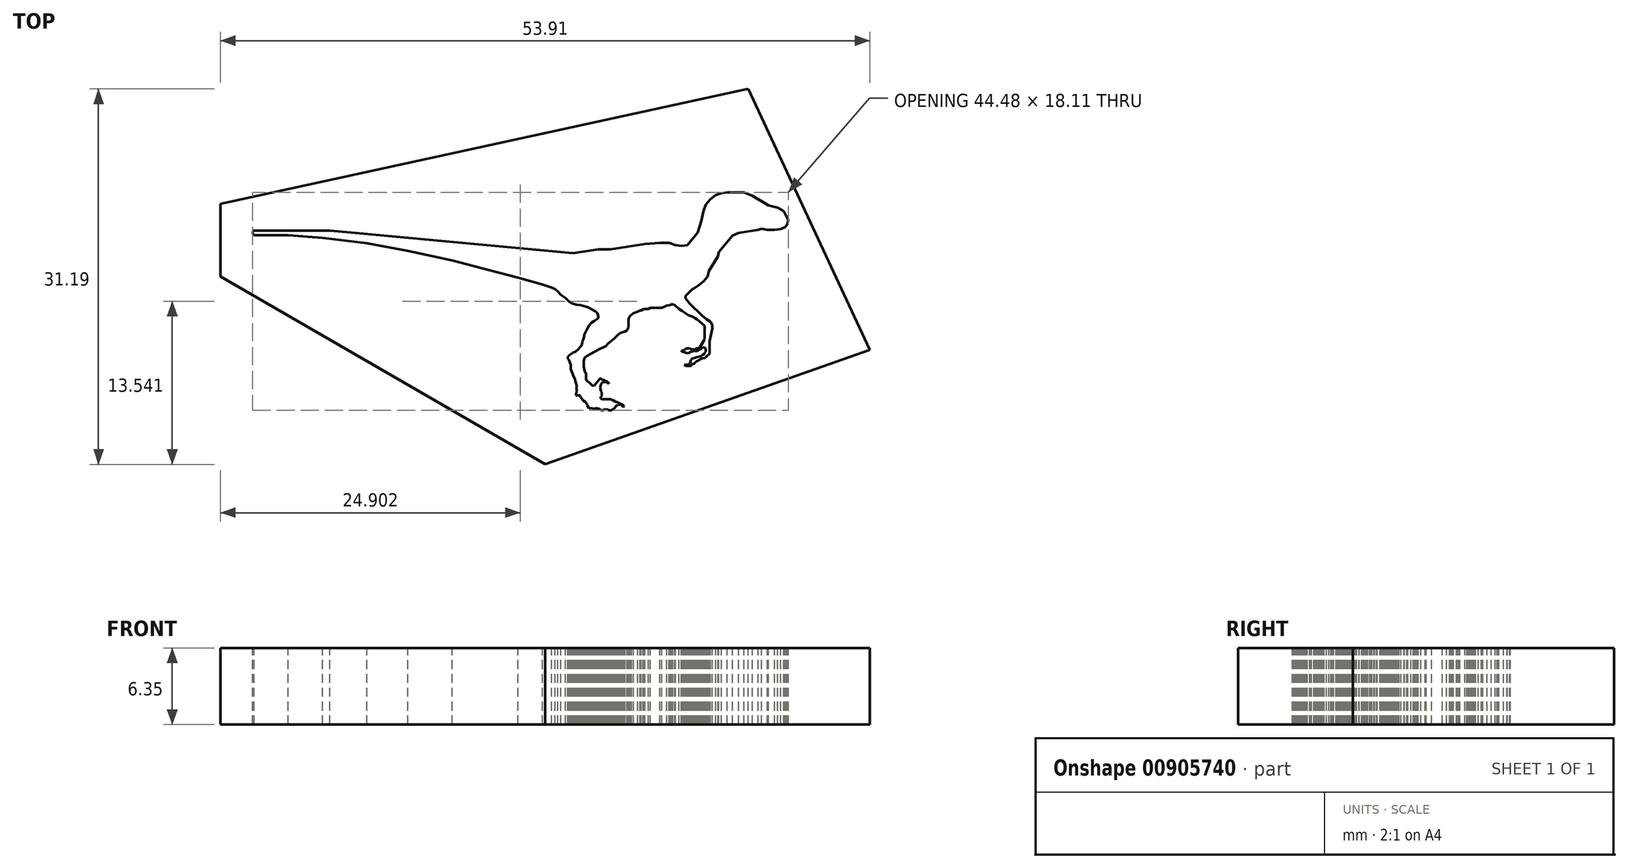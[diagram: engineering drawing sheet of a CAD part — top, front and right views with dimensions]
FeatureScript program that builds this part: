
annotation { "Feature Type Name" : "Feature", "Feature Type Description" : "" }
export const myFeature = defineFeature(function(context is Context, id is Id, definition is map)
    precondition{}
    {
        {
            var Q0;
            Q0=qCreatedBy(makeId("Top.planeOp"),FACE);
            var sketch = newSketch(context, id + "F0", { "sketchPlane" : qUnion([Q0])});
            skLineSegment(sketch, "E0", {"start": v(-51.18, -22.67) * mm, "end": v(-48.07, -22.67) * mm});
            skLineSegment(sketch, "E1", {"start": v(-48.07, -22.67) * mm, "end": v(-44.84, -22.67) * mm});
            skLineSegment(sketch, "E2", {"start": v(-44.84, -22.67) * mm, "end": v(-42.38, -22.91) * mm});
            skLineSegment(sketch, "E3", {"start": v(-42.38, -22.91) * mm, "end": v(-36.65, -23.44) * mm});
            skLineSegment(sketch, "E4", {"start": v(-36.65, -23.44) * mm, "end": v(-29.92, -24.07) * mm});
            skLineSegment(sketch, "E5", {"start": v(-29.92, -24.07) * mm, "end": v(-24.63, -24.56) * mm});
            skLineSegment(sketch, "E6", {"start": v(-24.63, -24.56) * mm, "end": v(-23.02, -24.3) * mm});
            skLineSegment(sketch, "E7", {"start": v(-23.02, -24.3) * mm, "end": v(-22.54, -24.23) * mm});
            skLineSegment(sketch, "E8", {"start": v(-22.54, -24.23) * mm, "end": v(-21.51, -24.23) * mm});
            skLineSegment(sketch, "E9", {"start": v(-21.51, -24.23) * mm, "end": v(-20.6, -24.1) * mm});
            skLineSegment(sketch, "E10", {"start": v(-20.6, -24.1) * mm, "end": v(-18.67, -23.8) * mm});
            skLineSegment(sketch, "E11", {"start": v(-18.67, -23.8) * mm, "end": v(-17.43, -23.7) * mm});
            skLineSegment(sketch, "E12", {"start": v(-17.43, -23.7) * mm, "end": v(-16.67, -23.7) * mm});
            skLineSegment(sketch, "E13", {"start": v(-16.67, -23.7) * mm, "end": v(-16.12, -23.88) * mm});
            skLineSegment(sketch, "E14", {"start": v(-16.12, -23.88) * mm, "end": v(-15.62, -23.96) * mm});
            skLineSegment(sketch, "E15", {"start": v(-15.62, -23.96) * mm, "end": v(-15.15, -23.89) * mm});
            skLineSegment(sketch, "E16", {"start": v(-15.15, -23.89) * mm, "end": v(-14.64, -23.27) * mm});
            skLineSegment(sketch, "E17", {"start": v(-14.64, -23.27) * mm, "end": v(-14.27, -22.84) * mm});
            skLineSegment(sketch, "E18", {"start": v(-14.27, -22.84) * mm, "end": v(-14.02, -21.91) * mm});
            skLineSegment(sketch, "E19", {"start": v(-14.02, -21.91) * mm, "end": v(-13.82, -21.07) * mm});
            skLineSegment(sketch, "E20", {"start": v(-13.82, -21.07) * mm, "end": v(-13.62, -20.52) * mm});
            skLineSegment(sketch, "E21", {"start": v(-13.62, -20.52) * mm, "end": v(-13.25, -20.08) * mm});
            skLineSegment(sketch, "E22", {"start": v(-13.25, -20.08) * mm, "end": v(-12.78, -19.74) * mm});
            skLineSegment(sketch, "E23", {"start": v(-12.78, -19.74) * mm, "end": v(-12.33, -19.58) * mm});
            skLineSegment(sketch, "E24", {"start": v(-12.33, -19.58) * mm, "end": v(-11.85, -19.5) * mm});
            skLineSegment(sketch, "E25", {"start": v(-11.85, -19.5) * mm, "end": v(-11.24, -19.5) * mm});
            skLineSegment(sketch, "E26", {"start": v(-11.24, -19.5) * mm, "end": v(-10.44, -19.5) * mm});
            skLineSegment(sketch, "E27", {"start": v(-10.44, -19.5) * mm, "end": v(-9.76, -19.8) * mm});
            skLineSegment(sketch, "E28", {"start": v(-9.76, -19.8) * mm, "end": v(-9.18, -20.15) * mm});
            skLineSegment(sketch, "E29", {"start": v(-9.18, -20.15) * mm, "end": v(-8.72, -20.42) * mm});
            skLineSegment(sketch, "E30", {"start": v(-8.72, -20.42) * mm, "end": v(-8.41, -20.6) * mm});
            skLineSegment(sketch, "E31", {"start": v(-8.41, -20.6) * mm, "end": v(-8.14, -20.66) * mm});
            skLineSegment(sketch, "E32", {"start": v(-8.14, -20.66) * mm, "end": v(-7.64, -20.78) * mm});
            skLineSegment(sketch, "E33", {"start": v(-7.64, -20.78) * mm, "end": v(-7.15, -21.07) * mm});
            skLineSegment(sketch, "E34", {"start": v(-7.15, -21.07) * mm, "end": v(-6.95, -21.43) * mm});
            skLineSegment(sketch, "E35", {"start": v(-6.95, -21.43) * mm, "end": v(-6.77, -21.8) * mm});
            skLineSegment(sketch, "E36", {"start": v(-6.77, -21.8) * mm, "end": v(-6.86, -22.17) * mm});
            skLineSegment(sketch, "E37", {"start": v(-6.86, -22.17) * mm, "end": v(-7.05, -22.4) * mm});
            skLineSegment(sketch, "E38", {"start": v(-7.05, -22.4) * mm, "end": v(-7.39, -22.55) * mm});
            skLineSegment(sketch, "E39", {"start": v(-7.39, -22.55) * mm, "end": v(-7.9, -22.63) * mm});
            skLineSegment(sketch, "E40", {"start": v(-7.9, -22.63) * mm, "end": v(-8.5, -22.63) * mm});
            skLineSegment(sketch, "E41", {"start": v(-8.5, -22.63) * mm, "end": v(-8.99, -22.52) * mm});
            skLineSegment(sketch, "E42", {"start": v(-8.99, -22.52) * mm, "end": v(-9.29, -22.63) * mm});
            skLineSegment(sketch, "E43", {"start": v(-9.29, -22.63) * mm, "end": v(-9.7, -22.7) * mm});
            skLineSegment(sketch, "E44", {"start": v(-9.7, -22.7) * mm, "end": v(-10.44, -22.81) * mm});
            skLineSegment(sketch, "E45", {"start": v(-10.44, -22.81) * mm, "end": v(-10.89, -22.88) * mm});
            skLineSegment(sketch, "E46", {"start": v(-10.89, -22.88) * mm, "end": v(-11.4, -23.1) * mm});
            skLineSegment(sketch, "E47", {"start": v(-11.4, -23.1) * mm, "end": v(-12.04, -23.86) * mm});
            skLineSegment(sketch, "E48", {"start": v(-12.04, -23.86) * mm, "end": v(-12.54, -24.46) * mm});
            skLineSegment(sketch, "E49", {"start": v(-12.54, -24.46) * mm, "end": v(-12.62, -24.81) * mm});
            skLineSegment(sketch, "E50", {"start": v(-12.62, -24.81) * mm, "end": v(-13.07, -25.57) * mm});
            skLineSegment(sketch, "E51", {"start": v(-13.07, -25.57) * mm, "end": v(-13.36, -26.05) * mm});
            skLineSegment(sketch, "E52", {"start": v(-13.36, -26.05) * mm, "end": v(-13.46, -26.49) * mm});
            skLineSegment(sketch, "E53", {"start": v(-13.46, -26.49) * mm, "end": v(-13.82, -26.92) * mm});
            skLineSegment(sketch, "E54", {"start": v(-13.82, -26.92) * mm, "end": v(-14.25, -27.26) * mm});
            skLineSegment(sketch, "E55", {"start": v(-14.25, -27.26) * mm, "end": v(-14.54, -27.45) * mm});
            skLineSegment(sketch, "E56", {"start": v(-14.54, -27.45) * mm, "end": v(-14.77, -27.57) * mm});
            skLineSegment(sketch, "E57", {"start": v(-14.77, -27.57) * mm, "end": v(-15.31, -28.12) * mm});
            skLineSegment(sketch, "E58", {"start": v(-15.31, -28.12) * mm, "end": v(-15.31, -28.32) * mm});
            skLineSegment(sketch, "E59", {"start": v(-15.31, -28.32) * mm, "end": v(-14.96, -28.73) * mm});
            skLineSegment(sketch, "E60", {"start": v(-14.96, -28.73) * mm, "end": v(-13.95, -29.72) * mm});
            skLineSegment(sketch, "E61", {"start": v(-13.95, -29.72) * mm, "end": v(-13.56, -30.04) * mm});
            skLineSegment(sketch, "E62", {"start": v(-13.56, -30.04) * mm, "end": v(-13.23, -30.24) * mm});
            skLineSegment(sketch, "E63", {"start": v(-13.23, -30.24) * mm, "end": v(-13.07, -30.54) * mm});
            skLineSegment(sketch, "E64", {"start": v(-13.07, -30.54) * mm, "end": v(-13.07, -30.85) * mm});
            skLineSegment(sketch, "E65", {"start": v(-13.07, -30.85) * mm, "end": v(-13.17, -31.24) * mm});
            skLineSegment(sketch, "E66", {"start": v(-13.17, -31.24) * mm, "end": v(-13.3, -31.85) * mm});
            skLineSegment(sketch, "E67", {"start": v(-13.3, -31.85) * mm, "end": v(-13.3, -32.58) * mm});
            skLineSegment(sketch, "E68", {"start": v(-13.3, -32.58) * mm, "end": v(-13.3, -32.91) * mm});
            skLineSegment(sketch, "E69", {"start": v(-13.3, -32.91) * mm, "end": v(-13.6, -33.17) * mm});
            skLineSegment(sketch, "E70", {"start": v(-13.6, -33.17) * mm, "end": v(-13.67, -33.25) * mm});
            skLineSegment(sketch, "E71", {"start": v(-13.67, -33.25) * mm, "end": v(-13.9, -33.29) * mm});
            skLineSegment(sketch, "E72", {"start": v(-13.9, -33.29) * mm, "end": v(-14.13, -33.4) * mm});
            skLineSegment(sketch, "E73", {"start": v(-14.13, -33.4) * mm, "end": v(-14.4, -33.55) * mm});
            skLineSegment(sketch, "E74", {"start": v(-14.4, -33.55) * mm, "end": v(-14.52, -33.65) * mm});
            skLineSegment(sketch, "E75", {"start": v(-14.52, -33.65) * mm, "end": v(-14.59, -33.74) * mm});
            skLineSegment(sketch, "E76", {"start": v(-14.59, -33.74) * mm, "end": v(-14.72, -33.76) * mm});
            skLineSegment(sketch, "E77", {"start": v(-14.72, -33.76) * mm, "end": v(-14.86, -33.92) * mm});
            skLineSegment(sketch, "E78", {"start": v(-14.86, -33.92) * mm, "end": v(-15.24, -33.92) * mm});
            skLineSegment(sketch, "E79", {"start": v(-15.24, -33.92) * mm, "end": v(-15.4, -33.83) * mm});
            skLineSegment(sketch, "E80", {"start": v(-15.4, -33.83) * mm, "end": v(-15.06, -33.83) * mm});
            skLineSegment(sketch, "E81", {"start": v(-15.06, -33.83) * mm, "end": v(-14.91, -33.65) * mm});
            skLineSegment(sketch, "E82", {"start": v(-14.91, -33.65) * mm, "end": v(-14.86, -33.44) * mm});
            skLineSegment(sketch, "E83", {"start": v(-14.86, -33.44) * mm, "end": v(-14.77, -33.33) * mm});
            skLineSegment(sketch, "E84", {"start": v(-14.77, -33.33) * mm, "end": v(-14.56, -33.26) * mm});
            skLineSegment(sketch, "E85", {"start": v(-14.56, -33.26) * mm, "end": v(-14.35, -33.18) * mm});
            skLineSegment(sketch, "E86", {"start": v(-14.35, -33.18) * mm, "end": v(-14.08, -33.14) * mm});
            skLineSegment(sketch, "E87", {"start": v(-14.08, -33.14) * mm, "end": v(-13.87, -33) * mm});
            skLineSegment(sketch, "E88", {"start": v(-13.87, -33) * mm, "end": v(-13.72, -32.91) * mm});
            skLineSegment(sketch, "E89", {"start": v(-13.72, -32.91) * mm, "end": v(-13.69, -32.78) * mm});
            skLineSegment(sketch, "E90", {"start": v(-13.69, -32.78) * mm, "end": v(-13.63, -32.75) * mm});
            skLineSegment(sketch, "E91", {"start": v(-13.63, -32.75) * mm, "end": v(-13.63, -32.5) * mm});
            skLineSegment(sketch, "E92", {"start": v(-13.63, -32.5) * mm, "end": v(-13.68, -32.43) * mm});
            skLineSegment(sketch, "E93", {"start": v(-13.68, -32.43) * mm, "end": v(-13.75, -32.39) * mm});
            skLineSegment(sketch, "E94", {"start": v(-13.75, -32.39) * mm, "end": v(-13.85, -32.37) * mm});
            skLineSegment(sketch, "E95", {"start": v(-13.85, -32.37) * mm, "end": v(-13.99, -32.48) * mm});
            skLineSegment(sketch, "E96", {"start": v(-13.99, -32.48) * mm, "end": v(-14.18, -32.58) * mm});
            skLineSegment(sketch, "E97", {"start": v(-14.18, -32.58) * mm, "end": v(-14.35, -32.73) * mm});
            skLineSegment(sketch, "E98", {"start": v(-14.35, -32.73) * mm, "end": v(-14.5, -32.7) * mm});
            skLineSegment(sketch, "E99", {"start": v(-14.5, -32.7) * mm, "end": v(-14.57, -32.66) * mm});
            skLineSegment(sketch, "E100", {"start": v(-14.57, -32.66) * mm, "end": v(-14.68, -32.68) * mm});
            skPoint(sketch, "E100.endSnap0", {"position": v(-14.54, -32.68) * mm});
            skLineSegment(sketch, "E101", {"start": v(-14.68, -32.68) * mm, "end": v(-14.7, -32.73) * mm});
            skLineSegment(sketch, "E102", {"start": v(-14.7, -32.73) * mm, "end": v(-14.88, -32.76) * mm});
            skLineSegment(sketch, "E103", {"start": v(-14.88, -32.76) * mm, "end": v(-15, -32.82) * mm});
            skLineSegment(sketch, "E104", {"start": v(-15, -32.82) * mm, "end": v(-15.1, -32.91) * mm});
            skLineSegment(sketch, "E105", {"start": v(-15.1, -32.91) * mm, "end": v(-15.2, -32.86) * mm});
            skLineSegment(sketch, "E106", {"start": v(-15.2, -32.86) * mm, "end": v(-15.53, -32.75) * mm});
            skLineSegment(sketch, "E107", {"start": v(-15.53, -32.75) * mm, "end": v(-15.63, -32.72) * mm});
            skLineSegment(sketch, "E108", {"start": v(-15.63, -32.72) * mm, "end": v(-15.64, -32.66) * mm});
            skLineSegment(sketch, "E109", {"start": v(-15.64, -32.66) * mm, "end": v(-15.43, -32.63) * mm});
            skLineSegment(sketch, "E110", {"start": v(-15.43, -32.63) * mm, "end": v(-15.23, -32.45) * mm});
            skLineSegment(sketch, "E111", {"start": v(-15.23, -32.45) * mm, "end": v(-15.03, -32.45) * mm});
            skLineSegment(sketch, "E112", {"start": v(-15.03, -32.45) * mm, "end": v(-14.88, -32.49) * mm});
            skLineSegment(sketch, "E113", {"start": v(-14.88, -32.49) * mm, "end": v(-14.77, -32.55) * mm});
            skLineSegment(sketch, "E114", {"start": v(-14.77, -32.55) * mm, "end": v(-14.64, -32.53) * mm});
            skLineSegment(sketch, "E115", {"start": v(-14.64, -32.53) * mm, "end": v(-14.52, -32.56) * mm});
            skLineSegment(sketch, "E116", {"start": v(-14.52, -32.56) * mm, "end": v(-14.46, -32.52) * mm});
            skLineSegment(sketch, "E117", {"start": v(-14.46, -32.52) * mm, "end": v(-14.35, -32.47) * mm});
            skLineSegment(sketch, "E118", {"start": v(-14.35, -32.47) * mm, "end": v(-14.13, -32.38) * mm});
            skLineSegment(sketch, "E119", {"start": v(-14.13, -32.38) * mm, "end": v(-14, -32.18) * mm});
            skLineSegment(sketch, "E120", {"start": v(-14, -32.18) * mm, "end": v(-13.91, -32.01) * mm});
            skLineSegment(sketch, "E121", {"start": v(-13.91, -32.01) * mm, "end": v(-13.82, -31.87) * mm});
            skLineSegment(sketch, "E122", {"start": v(-13.82, -31.87) * mm, "end": v(-13.76, -31.76) * mm});
            skLineSegment(sketch, "E123", {"start": v(-13.76, -31.76) * mm, "end": v(-13.72, -31.59) * mm});
            skLineSegment(sketch, "E124", {"start": v(-13.72, -31.59) * mm, "end": v(-13.72, -30.9) * mm});
            skLineSegment(sketch, "E125", {"start": v(-13.72, -30.9) * mm, "end": v(-13.72, -30.6) * mm});
            skLineSegment(sketch, "E126", {"start": v(-13.72, -30.6) * mm, "end": v(-14.34, -30.06) * mm});
            skLineSegment(sketch, "E127", {"start": v(-14.34, -30.06) * mm, "end": v(-14.52, -29.96) * mm});
            skLineSegment(sketch, "E128", {"start": v(-14.52, -29.96) * mm, "end": v(-14.73, -29.84) * mm});
            skLineSegment(sketch, "E129", {"start": v(-14.73, -29.84) * mm, "end": v(-15.08, -29.7) * mm});
            skLineSegment(sketch, "E130", {"start": v(-15.08, -29.7) * mm, "end": v(-15.3, -29.53) * mm});
            skLineSegment(sketch, "E131", {"start": v(-15.3, -29.53) * mm, "end": v(-15.58, -29.36) * mm});
            skLineSegment(sketch, "E132", {"start": v(-15.58, -29.36) * mm, "end": v(-15.83, -29.2) * mm});
            skLineSegment(sketch, "E133", {"start": v(-15.83, -29.2) * mm, "end": v(-16.18, -28.87) * mm});
            skLineSegment(sketch, "E134", {"start": v(-16.18, -28.87) * mm, "end": v(-16.34, -28.8) * mm});
            skLineSegment(sketch, "E135", {"start": v(-16.34, -28.8) * mm, "end": v(-16.48, -28.8) * mm});
            skLineSegment(sketch, "E136", {"start": v(-16.48, -28.8) * mm, "end": v(-16.6, -28.86) * mm});
            skLineSegment(sketch, "E137", {"start": v(-16.6, -28.86) * mm, "end": v(-16.86, -28.91) * mm});
            skLineSegment(sketch, "E138", {"start": v(-16.86, -28.91) * mm, "end": v(-17.04, -29) * mm});
            skLineSegment(sketch, "E139", {"start": v(-17.04, -29) * mm, "end": v(-17.28, -29.1) * mm});
            skLineSegment(sketch, "E140", {"start": v(-17.28, -29.1) * mm, "end": v(-17.74, -29.1) * mm});
            skLineSegment(sketch, "E141", {"start": v(-17.74, -29.1) * mm, "end": v(-18.05, -29.1) * mm});
            skLineSegment(sketch, "E142", {"start": v(-18.05, -29.1) * mm, "end": v(-18.24, -29.1) * mm});
            skLineSegment(sketch, "E143", {"start": v(-18.24, -29.1) * mm, "end": v(-18.37, -29.18) * mm});
            skLineSegment(sketch, "E144", {"start": v(-18.37, -29.18) * mm, "end": v(-18.53, -29.18) * mm});
            skLineSegment(sketch, "E145", {"start": v(-18.53, -29.18) * mm, "end": v(-18.73, -29.18) * mm});
            skLineSegment(sketch, "E146", {"start": v(-18.73, -29.18) * mm, "end": v(-18.83, -29.2) * mm});
            skLineSegment(sketch, "E147", {"start": v(-18.83, -29.2) * mm, "end": v(-18.99, -29.3) * mm});
            skLineSegment(sketch, "E148", {"start": v(-18.99, -29.3) * mm, "end": v(-19.1, -29.3) * mm});
            skLineSegment(sketch, "E149", {"start": v(-19.1, -29.3) * mm, "end": v(-19.28, -29.4) * mm});
            skLineSegment(sketch, "E150", {"start": v(-19.28, -29.4) * mm, "end": v(-19.61, -29.56) * mm});
            skLineSegment(sketch, "E151", {"start": v(-19.61, -29.56) * mm, "end": v(-19.78, -29.66) * mm});
            skLineSegment(sketch, "E152", {"start": v(-19.78, -29.66) * mm, "end": v(-19.9, -29.76) * mm});
            skLineSegment(sketch, "E153", {"start": v(-19.9, -29.76) * mm, "end": v(-20.05, -30.02) * mm});
            skLineSegment(sketch, "E154", {"start": v(-20.05, -30.02) * mm, "end": v(-20.05, -30.18) * mm});
            skLineSegment(sketch, "E155", {"start": v(-20.05, -30.18) * mm, "end": v(-20.05, -30.6) * mm});
            skLineSegment(sketch, "E156", {"start": v(-20.05, -30.6) * mm, "end": v(-20.08, -30.78) * mm});
            skLineSegment(sketch, "E157", {"start": v(-20.08, -30.78) * mm, "end": v(-20.16, -30.98) * mm});
            skLineSegment(sketch, "E158", {"start": v(-20.16, -30.98) * mm, "end": v(-20.32, -31.06) * mm});
            skLineSegment(sketch, "E159", {"start": v(-20.32, -31.06) * mm, "end": v(-20.53, -31.12) * mm});
            skLineSegment(sketch, "E160", {"start": v(-20.53, -31.12) * mm, "end": v(-20.74, -31.18) * mm});
            skLineSegment(sketch, "E161", {"start": v(-20.74, -31.18) * mm, "end": v(-20.94, -31.36) * mm});
            skLineSegment(sketch, "E162", {"start": v(-20.94, -31.36) * mm, "end": v(-21.2, -31.62) * mm});
            skLineSegment(sketch, "E163", {"start": v(-21.2, -31.62) * mm, "end": v(-21.76, -32.07) * mm});
            skLineSegment(sketch, "E164", {"start": v(-21.76, -32.07) * mm, "end": v(-21.92, -32.28) * mm});
            skLineSegment(sketch, "E165", {"start": v(-21.92, -32.28) * mm, "end": v(-22.5, -32.56) * mm});
            skLineSegment(sketch, "E166", {"start": v(-22.5, -32.56) * mm, "end": v(-23.14, -32.9) * mm});
            skLineSegment(sketch, "E167", {"start": v(-23.14, -32.9) * mm, "end": v(-23.5, -33.09) * mm});
            skLineSegment(sketch, "E168", {"start": v(-23.5, -33.09) * mm, "end": v(-23.7, -33.27) * mm});
            skLineSegment(sketch, "E169", {"start": v(-23.7, -33.27) * mm, "end": v(-23.75, -33.53) * mm});
            skLineSegment(sketch, "E170", {"start": v(-23.75, -33.53) * mm, "end": v(-23.75, -33.98) * mm});
            skLineSegment(sketch, "E171", {"start": v(-23.75, -33.98) * mm, "end": v(-23.69, -34.3) * mm});
            skLineSegment(sketch, "E172", {"start": v(-23.69, -34.3) * mm, "end": v(-23.55, -34.58) * mm});
            skLineSegment(sketch, "E173", {"start": v(-23.55, -34.58) * mm, "end": v(-23.55, -34.74) * mm});
            skLineSegment(sketch, "E174", {"start": v(-23.55, -34.74) * mm, "end": v(-23.55, -35) * mm});
            skLineSegment(sketch, "E175", {"start": v(-23.55, -35) * mm, "end": v(-23.48, -35.15) * mm});
            skLineSegment(sketch, "E176", {"start": v(-23.48, -35.15) * mm, "end": v(-23.26, -35.32) * mm});
            skLineSegment(sketch, "E177", {"start": v(-23.26, -35.32) * mm, "end": v(-23.04, -35.54) * mm});
            skLineSegment(sketch, "E178", {"start": v(-23.04, -35.54) * mm, "end": v(-22.9, -35.58) * mm});
            skLineSegment(sketch, "E179", {"start": v(-22.9, -35.58) * mm, "end": v(-22.69, -35.3) * mm});
            skLineSegment(sketch, "E180", {"start": v(-22.69, -35.3) * mm, "end": v(-22.58, -35.16) * mm});
            skLineSegment(sketch, "E181", {"start": v(-22.58, -35.16) * mm, "end": v(-22.5, -35.05) * mm});
            skLineSegment(sketch, "E182", {"start": v(-22.5, -35.05) * mm, "end": v(-22.4, -34.97) * mm});
            skLineSegment(sketch, "E183", {"start": v(-22.4, -34.97) * mm, "end": v(-22.32, -34.97) * mm});
            skLineSegment(sketch, "E184", {"start": v(-22.32, -34.97) * mm, "end": v(-22.21, -35.05) * mm});
            skLineSegment(sketch, "E185", {"start": v(-22.21, -35.05) * mm, "end": v(-22.06, -35.09) * mm});
            skLineSegment(sketch, "E186", {"start": v(-22.06, -35.09) * mm, "end": v(-21.98, -35.15) * mm});
            skLineSegment(sketch, "E187", {"start": v(-21.98, -35.15) * mm, "end": v(-21.85, -35.18) * mm});
            skLineSegment(sketch, "E188", {"start": v(-21.85, -35.18) * mm, "end": v(-21.64, -35.34) * mm});
            skLineSegment(sketch, "E189", {"start": v(-21.64, -35.34) * mm, "end": v(-21.66, -35.38) * mm});
            skLineSegment(sketch, "E190", {"start": v(-21.66, -35.38) * mm, "end": v(-21.82, -35.29) * mm});
            skLineSegment(sketch, "E191", {"start": v(-21.82, -35.29) * mm, "end": v(-21.9, -35.26) * mm});
            skLineSegment(sketch, "E192", {"start": v(-21.9, -35.26) * mm, "end": v(-22.04, -35.26) * mm});
            skLineSegment(sketch, "E193", {"start": v(-22.04, -35.26) * mm, "end": v(-22.14, -35.26) * mm});
            skLineSegment(sketch, "E194", {"start": v(-22.14, -35.26) * mm, "end": v(-22.26, -35.34) * mm});
            skLineSegment(sketch, "E195", {"start": v(-22.26, -35.34) * mm, "end": v(-22.34, -35.43) * mm});
            skLineSegment(sketch, "E196", {"start": v(-22.34, -35.43) * mm, "end": v(-22.36, -35.55) * mm});
            skLineSegment(sketch, "E197", {"start": v(-22.36, -35.55) * mm, "end": v(-22.4, -35.72) * mm});
            skLineSegment(sketch, "E198", {"start": v(-22.4, -35.72) * mm, "end": v(-22.31, -36) * mm});
            skLineSegment(sketch, "E199", {"start": v(-22.31, -36) * mm, "end": v(-22.25, -36.13) * mm});
            skLineSegment(sketch, "E200", {"start": v(-22.25, -36.13) * mm, "end": v(-22.25, -36.27) * mm});
            skLineSegment(sketch, "E201", {"start": v(-22.25, -36.27) * mm, "end": v(-22.25, -36.4) * mm});
            skLineSegment(sketch, "E202", {"start": v(-22.25, -36.4) * mm, "end": v(-22.34, -36.5) * mm});
            skLineSegment(sketch, "E203", {"start": v(-22.34, -36.5) * mm, "end": v(-22.35, -36.56) * mm});
            skLineSegment(sketch, "E204", {"start": v(-22.35, -36.56) * mm, "end": v(-22.35, -36.61) * mm});
            skLineSegment(sketch, "E205", {"start": v(-22.35, -36.61) * mm, "end": v(-22.3, -36.65) * mm});
            skLineSegment(sketch, "E206", {"start": v(-22.3, -36.65) * mm, "end": v(-22.23, -36.68) * mm});
            skLineSegment(sketch, "E207", {"start": v(-22.23, -36.68) * mm, "end": v(-21.98, -36.68) * mm});
            skLineSegment(sketch, "E208", {"start": v(-21.98, -36.68) * mm, "end": v(-21.7, -36.67) * mm});
            skLineSegment(sketch, "E209", {"start": v(-21.7, -36.67) * mm, "end": v(-21.57, -36.67) * mm});
            skLineSegment(sketch, "E210", {"start": v(-21.57, -36.67) * mm, "end": v(-21.32, -36.78) * mm});
            skLineSegment(sketch, "E211", {"start": v(-21.32, -36.78) * mm, "end": v(-21.14, -36.88) * mm});
            skLineSegment(sketch, "E212", {"start": v(-21.14, -36.88) * mm, "end": v(-20.97, -36.93) * mm});
            skLineSegment(sketch, "E213", {"start": v(-20.97, -36.93) * mm, "end": v(-20.9, -36.98) * mm});
            skLineSegment(sketch, "E214", {"start": v(-20.9, -36.98) * mm, "end": v(-20.76, -37.03) * mm});
            skLineSegment(sketch, "E215", {"start": v(-20.76, -37.03) * mm, "end": v(-20.56, -37.14) * mm});
            skLineSegment(sketch, "E216", {"start": v(-20.56, -37.14) * mm, "end": v(-20.47, -37.2) * mm});
            skLineSegment(sketch, "E217", {"start": v(-20.47, -37.2) * mm, "end": v(-20.37, -37.28) * mm});
            skLineSegment(sketch, "E218", {"start": v(-20.37, -37.28) * mm, "end": v(-20.41, -37.33) * mm});
            skLineSegment(sketch, "E219", {"start": v(-20.41, -37.33) * mm, "end": v(-20.51, -37.28) * mm});
            skLineSegment(sketch, "E220", {"start": v(-20.51, -37.28) * mm, "end": v(-20.59, -37.22) * mm});
            skLineSegment(sketch, "E221", {"start": v(-20.59, -37.22) * mm, "end": v(-20.66, -37.16) * mm});
            skLineSegment(sketch, "E222", {"start": v(-20.66, -37.16) * mm, "end": v(-20.76, -37.12) * mm});
            skLineSegment(sketch, "E223", {"start": v(-20.76, -37.12) * mm, "end": v(-20.82, -37.12) * mm});
            skLineSegment(sketch, "E224", {"start": v(-20.82, -37.12) * mm, "end": v(-20.87, -37.11) * mm});
            skLineSegment(sketch, "E225", {"start": v(-20.87, -37.11) * mm, "end": v(-20.92, -37.13) * mm});
            skLineSegment(sketch, "E226", {"start": v(-20.92, -37.13) * mm, "end": v(-20.96, -37.2) * mm});
            skLineSegment(sketch, "E227", {"start": v(-20.96, -37.2) * mm, "end": v(-21.04, -37.24) * mm});
            skLineSegment(sketch, "E228", {"start": v(-21.04, -37.24) * mm, "end": v(-21.1, -37.31) * mm});
            skLineSegment(sketch, "E229", {"start": v(-21.1, -37.31) * mm, "end": v(-21.23, -37.47) * mm});
            skLineSegment(sketch, "E230", {"start": v(-21.23, -37.47) * mm, "end": v(-21.38, -37.55) * mm});
            skLineSegment(sketch, "E231", {"start": v(-21.38, -37.55) * mm, "end": v(-21.42, -37.6) * mm});
            skLineSegment(sketch, "E232", {"start": v(-21.42, -37.6) * mm, "end": v(-21.55, -37.61) * mm});
            skLineSegment(sketch, "E233", {"start": v(-21.55, -37.61) * mm, "end": v(-21.67, -37.61) * mm});
            skLineSegment(sketch, "E234", {"start": v(-21.67, -37.61) * mm, "end": v(-21.7, -37.57) * mm});
            skLineSegment(sketch, "E235", {"start": v(-21.7, -37.57) * mm, "end": v(-21.78, -37.54) * mm});
            skLineSegment(sketch, "E236", {"start": v(-21.78, -37.54) * mm, "end": v(-21.95, -37.54) * mm});
            skLineSegment(sketch, "E237", {"start": v(-21.95, -37.54) * mm, "end": v(-22.03, -37.54) * mm});
            skLineSegment(sketch, "E238", {"start": v(-22.03, -37.54) * mm, "end": v(-22.1, -37.57) * mm});
            skLineSegment(sketch, "E239", {"start": v(-22.1, -37.57) * mm, "end": v(-22.15, -37.6) * mm});
            skLineSegment(sketch, "E240", {"start": v(-22.15, -37.6) * mm, "end": v(-22.25, -37.61) * mm});
            skLineSegment(sketch, "E241", {"start": v(-22.25, -37.61) * mm, "end": v(-22.31, -37.61) * mm});
            skLineSegment(sketch, "E242", {"start": v(-22.31, -37.61) * mm, "end": v(-22.37, -37.56) * mm});
            skLineSegment(sketch, "E243", {"start": v(-22.37, -37.56) * mm, "end": v(-22.45, -37.5) * mm});
            skLineSegment(sketch, "E244", {"start": v(-22.45, -37.5) * mm, "end": v(-22.55, -37.47) * mm});
            skLineSegment(sketch, "E245", {"start": v(-22.55, -37.47) * mm, "end": v(-22.62, -37.45) * mm});
            skLineSegment(sketch, "E246", {"start": v(-22.62, -37.45) * mm, "end": v(-22.7, -37.44) * mm});
            skLineSegment(sketch, "E247", {"start": v(-22.7, -37.44) * mm, "end": v(-22.79, -37.44) * mm});
            skLineSegment(sketch, "E248", {"start": v(-22.79, -37.44) * mm, "end": v(-22.83, -37.47) * mm});
            skLineSegment(sketch, "E249", {"start": v(-22.83, -37.47) * mm, "end": v(-22.98, -37.47) * mm});
            skLineSegment(sketch, "E250", {"start": v(-22.98, -37.47) * mm, "end": v(-23.04, -37.43) * mm});
            skLineSegment(sketch, "E251", {"start": v(-23.04, -37.43) * mm, "end": v(-23.23, -37.44) * mm});
            skLineSegment(sketch, "E252", {"start": v(-23.23, -37.44) * mm, "end": v(-23.32, -37.44) * mm});
            skLineSegment(sketch, "E253", {"start": v(-23.32, -37.44) * mm, "end": v(-23.45, -37.19) * mm});
            skLineSegment(sketch, "E254", {"start": v(-23.45, -37.19) * mm, "end": v(-23.49, -37.07) * mm});
            skLineSegment(sketch, "E255", {"start": v(-23.49, -37.07) * mm, "end": v(-23.64, -36.9) * mm});
            skLineSegment(sketch, "E256", {"start": v(-23.64, -36.9) * mm, "end": v(-23.8, -36.8) * mm});
            skLineSegment(sketch, "E257", {"start": v(-23.8, -36.8) * mm, "end": v(-23.87, -36.72) * mm});
            skLineSegment(sketch, "E258", {"start": v(-23.87, -36.72) * mm, "end": v(-23.92, -36.61) * mm});
            skLineSegment(sketch, "E259", {"start": v(-23.92, -36.61) * mm, "end": v(-24, -36.52) * mm});
            skLineSegment(sketch, "E260", {"start": v(-24, -36.52) * mm, "end": v(-24.04, -36.43) * mm});
            skLineSegment(sketch, "E261", {"start": v(-24.04, -36.43) * mm, "end": v(-24.11, -36.4) * mm});
            skLineSegment(sketch, "E262", {"start": v(-24.11, -36.4) * mm, "end": v(-24.19, -36.35) * mm});
            skLineSegment(sketch, "E263", {"start": v(-24.19, -36.35) * mm, "end": v(-24.26, -36.35) * mm});
            skLineSegment(sketch, "E264", {"start": v(-24.26, -36.35) * mm, "end": v(-24.3, -36.4) * mm});
            skLineSegment(sketch, "E265", {"start": v(-24.3, -36.4) * mm, "end": v(-24.38, -36.36) * mm});
            skLineSegment(sketch, "E266", {"start": v(-24.38, -36.36) * mm, "end": v(-24.39, -36.15) * mm});
            skLineSegment(sketch, "E267", {"start": v(-24.39, -36.15) * mm, "end": v(-24.36, -36.1) * mm});
            skLineSegment(sketch, "E268", {"start": v(-24.36, -36.1) * mm, "end": v(-24.33, -36) * mm});
            skLineSegment(sketch, "E269", {"start": v(-24.33, -36) * mm, "end": v(-24.35, -35.82) * mm});
            skLineSegment(sketch, "E270", {"start": v(-24.35, -35.82) * mm, "end": v(-24.35, -35.7) * mm});
            skLineSegment(sketch, "E271", {"start": v(-24.35, -35.7) * mm, "end": v(-24.33, -35.6) * mm});
            skLineSegment(sketch, "E272", {"start": v(-24.33, -35.6) * mm, "end": v(-24.37, -35.5) * mm});
            skLineSegment(sketch, "E273", {"start": v(-24.37, -35.5) * mm, "end": v(-24.4, -35.38) * mm});
            skLineSegment(sketch, "E274", {"start": v(-24.4, -35.38) * mm, "end": v(-24.46, -35.2) * mm});
            skLineSegment(sketch, "E275", {"start": v(-24.46, -35.2) * mm, "end": v(-24.47, -35) * mm});
            skLineSegment(sketch, "E276", {"start": v(-24.47, -35) * mm, "end": v(-24.6, -34.78) * mm});
            skLineSegment(sketch, "E277", {"start": v(-24.6, -34.78) * mm, "end": v(-24.66, -34.6) * mm});
            skLineSegment(sketch, "E278", {"start": v(-24.66, -34.6) * mm, "end": v(-24.74, -34.43) * mm});
            skLineSegment(sketch, "E279", {"start": v(-24.74, -34.43) * mm, "end": v(-24.8, -34.27) * mm});
            skLineSegment(sketch, "E280", {"start": v(-24.8, -34.27) * mm, "end": v(-24.83, -34.17) * mm});
            skLineSegment(sketch, "E281", {"start": v(-24.83, -34.17) * mm, "end": v(-24.84, -34.03) * mm});
            skLineSegment(sketch, "E282", {"start": v(-24.84, -34.03) * mm, "end": v(-24.84, -33.83) * mm});
            skLineSegment(sketch, "E283", {"start": v(-24.84, -33.83) * mm, "end": v(-24.9, -33.67) * mm});
            skLineSegment(sketch, "E284", {"start": v(-24.9, -33.67) * mm, "end": v(-24.99, -33.43) * mm});
            skLineSegment(sketch, "E285", {"start": v(-24.99, -33.43) * mm, "end": v(-25.07, -33.3) * mm});
            skLineSegment(sketch, "E286", {"start": v(-25.07, -33.3) * mm, "end": v(-25.07, -33.19) * mm});
            skLineSegment(sketch, "E287", {"start": v(-25.07, -33.19) * mm, "end": v(-25, -33.06) * mm});
            skLineSegment(sketch, "E288", {"start": v(-25, -33.06) * mm, "end": v(-24.86, -32.97) * mm});
            skLineSegment(sketch, "E289", {"start": v(-24.86, -32.97) * mm, "end": v(-24.73, -32.87) * mm});
            skLineSegment(sketch, "E290", {"start": v(-24.73, -32.87) * mm, "end": v(-24.64, -32.8) * mm});
            skLineSegment(sketch, "E291", {"start": v(-24.64, -32.8) * mm, "end": v(-24.45, -32.76) * mm});
            skLineSegment(sketch, "E292", {"start": v(-24.45, -32.76) * mm, "end": v(-24.34, -32.66) * mm});
            skLineSegment(sketch, "E293", {"start": v(-24.34, -32.66) * mm, "end": v(-24.2, -32.53) * mm});
            skLineSegment(sketch, "E294", {"start": v(-24.2, -32.53) * mm, "end": v(-24.07, -32.37) * mm});
            skLineSegment(sketch, "E295", {"start": v(-24.07, -32.37) * mm, "end": v(-23.93, -32.25) * mm});
            skLineSegment(sketch, "E296", {"start": v(-23.93, -32.25) * mm, "end": v(-23.87, -32.03) * mm});
            skLineSegment(sketch, "E297", {"start": v(-23.87, -32.03) * mm, "end": v(-23.85, -31.83) * mm});
            skLineSegment(sketch, "E298", {"start": v(-23.85, -31.83) * mm, "end": v(-23.78, -31.7) * mm});
            skLineSegment(sketch, "E299", {"start": v(-23.78, -31.7) * mm, "end": v(-23.73, -31.49) * mm});
            skLineSegment(sketch, "E300", {"start": v(-23.73, -31.49) * mm, "end": v(-23.73, -31.36) * mm});
            skLineSegment(sketch, "E301", {"start": v(-23.73, -31.36) * mm, "end": v(-23.59, -31.1) * mm});
            skLineSegment(sketch, "E302", {"start": v(-23.59, -31.1) * mm, "end": v(-23.45, -30.79) * mm});
            skLineSegment(sketch, "E303", {"start": v(-23.45, -30.79) * mm, "end": v(-23.32, -30.57) * mm});
            skLineSegment(sketch, "E304", {"start": v(-23.32, -30.57) * mm, "end": v(-23.13, -30.32) * mm});
            skLineSegment(sketch, "E305", {"start": v(-23.13, -30.32) * mm, "end": v(-22.87, -30.19) * mm});
            skLineSegment(sketch, "E306", {"start": v(-22.87, -30.19) * mm, "end": v(-22.66, -30.06) * mm});
            skLineSegment(sketch, "E307", {"start": v(-22.66, -30.06) * mm, "end": v(-22.55, -29.97) * mm});
            skLineSegment(sketch, "E308", {"start": v(-22.55, -29.97) * mm, "end": v(-22.54, -29.84) * mm});
            skLineSegment(sketch, "E309", {"start": v(-22.54, -29.84) * mm, "end": v(-22.58, -29.66) * mm});
            skLineSegment(sketch, "E310", {"start": v(-22.58, -29.66) * mm, "end": v(-22.64, -29.5) * mm});
            skLineSegment(sketch, "E311", {"start": v(-22.64, -29.5) * mm, "end": v(-22.8, -29.38) * mm});
            skLineSegment(sketch, "E312", {"start": v(-22.8, -29.38) * mm, "end": v(-23.14, -29.18) * mm});
            skLineSegment(sketch, "E313", {"start": v(-23.14, -29.18) * mm, "end": v(-23.36, -29.06) * mm});
            skLineSegment(sketch, "E314", {"start": v(-23.36, -29.06) * mm, "end": v(-23.56, -29.01) * mm});
            skLineSegment(sketch, "E315", {"start": v(-23.56, -29.01) * mm, "end": v(-24, -28.88) * mm});
            skLineSegment(sketch, "E316", {"start": v(-24, -28.88) * mm, "end": v(-24.3, -28.85) * mm});
            skLineSegment(sketch, "E317", {"start": v(-24.3, -28.85) * mm, "end": v(-24.66, -28.74) * mm});
            skLineSegment(sketch, "E318", {"start": v(-24.66, -28.74) * mm, "end": v(-24.97, -28.58) * mm});
            skLineSegment(sketch, "E319", {"start": v(-24.97, -28.58) * mm, "end": v(-25.28, -28.29) * mm});
            skLineSegment(sketch, "E320", {"start": v(-25.28, -28.29) * mm, "end": v(-25.64, -28) * mm});
            skLineSegment(sketch, "E321", {"start": v(-25.64, -28) * mm, "end": v(-25.9, -27.75) * mm});
            skLineSegment(sketch, "E322", {"start": v(-25.9, -27.75) * mm, "end": v(-26.12, -27.55) * mm});
            skLineSegment(sketch, "E323", {"start": v(-26.12, -27.55) * mm, "end": v(-26.43, -27.4) * mm});
            skLineSegment(sketch, "E324", {"start": v(-26.43, -27.4) * mm, "end": v(-27.18, -27.16) * mm});
            skLineSegment(sketch, "E325", {"start": v(-27.18, -27.16) * mm, "end": v(-29.22, -26.58) * mm});
            skLineSegment(sketch, "E326", {"start": v(-29.22, -26.58) * mm, "end": v(-31.64, -25.97) * mm});
            skLineSegment(sketch, "E327", {"start": v(-31.64, -25.97) * mm, "end": v(-34.69, -25.16) * mm});
            skLineSegment(sketch, "E328", {"start": v(-34.69, -25.16) * mm, "end": v(-38.37, -24.36) * mm});
            skLineSegment(sketch, "E329", {"start": v(-38.37, -24.36) * mm, "end": v(-41.77, -23.75) * mm});
            skLineSegment(sketch, "E330", {"start": v(-41.77, -23.75) * mm, "end": v(-45.45, -23.27) * mm});
            skLineSegment(sketch, "E331", {"start": v(-45.45, -23.27) * mm, "end": v(-48.3, -23.05) * mm});
            skLineSegment(sketch, "E332", {"start": v(-48.3, -23.05) * mm, "end": v(-51.13, -23.05) * mm});
            skLineSegment(sketch, "E333", {"start": v(-51.13, -23.05) * mm, "end": v(-51.22, -22.95) * mm});
            skLineSegment(sketch, "E334", {"start": v(-51.22, -22.95) * mm, "end": v(-51.25, -22.81) * mm});
            skLineSegment(sketch, "E335", {"start": v(-51.25, -22.81) * mm, "end": v(-51.18, -22.67) * mm});
            skLineSegment(sketch, "E336", {"start": v(-53.91, -10.9) * mm, "end": v(0, -10.9) * mm});
            skLineSegment(sketch, "E337", {"start": v(0, -10.9) * mm, "end": v(0, -42.1) * mm});
            skLineSegment(sketch, "E338", {"start": v(0, -42.1) * mm, "end": v(-53.91, -42.1) * mm});
            skLineSegment(sketch, "E339", {"start": v(-53.91, -42.1) * mm, "end": v(-53.91, -10.9) * mm});
            skSolve(sketch);
        }
        {
            var Q0;
            Q0=makeQuery(id+"F0.imprint","IMPRINT",FACE,{"disambiguationData":[TD([[makeQuery(id+"F0.imprint","IMPRINT",EDGE,{"derivedFrom":sQuery(id+"F0.wireOp",EDGE,"E0")}),1.0]])]});
            extrude(context, id + "F1", {"entities" : qUnion([Q0]), "oppositeDirection" : true, "depth" : 6.35 * mm, "offsetDistance" : 25.4 * mm});
        }
        {
            var Q0;
            Q0=makeQuery(id+"F1.opExtrude","CAP_FACE",FACE,{"disambiguationData":[OSD([sQuery(id+"F0.wireOp",EDGE,"E0"),sQuery(id+"F0.wireOp",EDGE,"E1"),sQuery(id+"F0.wireOp",EDGE,"E2"),sQuery(id+"F0.wireOp",EDGE,"E3"),sQuery(id+"F0.wireOp",EDGE,"E4"),sQuery(id+"F0.wireOp",EDGE,"E5"),sQuery(id+"F0.wireOp",EDGE,"E6"),sQuery(id+"F0.wireOp",EDGE,"E7"),sQuery(id+"F0.wireOp",EDGE,"E8"),sQuery(id+"F0.wireOp",EDGE,"E9"),sQuery(id+"F0.wireOp",EDGE,"E10"),sQuery(id+"F0.wireOp",EDGE,"E11"),sQuery(id+"F0.wireOp",EDGE,"E12"),sQuery(id+"F0.wireOp",EDGE,"E13"),sQuery(id+"F0.wireOp",EDGE,"E14"),sQuery(id+"F0.wireOp",EDGE,"E15"),sQuery(id+"F0.wireOp",EDGE,"E16"),sQuery(id+"F0.wireOp",EDGE,"E17"),sQuery(id+"F0.wireOp",EDGE,"E18"),sQuery(id+"F0.wireOp",EDGE,"E19"),sQuery(id+"F0.wireOp",EDGE,"E20"),sQuery(id+"F0.wireOp",EDGE,"E21"),sQuery(id+"F0.wireOp",EDGE,"E22"),sQuery(id+"F0.wireOp",EDGE,"E23"),sQuery(id+"F0.wireOp",EDGE,"E24"),sQuery(id+"F0.wireOp",EDGE,"E25"),sQuery(id+"F0.wireOp",EDGE,"E26"),sQuery(id+"F0.wireOp",EDGE,"E27"),sQuery(id+"F0.wireOp",EDGE,"E28"),sQuery(id+"F0.wireOp",EDGE,"E29"),sQuery(id+"F0.wireOp",EDGE,"E30"),sQuery(id+"F0.wireOp",EDGE,"E31"),sQuery(id+"F0.wireOp",EDGE,"E32"),sQuery(id+"F0.wireOp",EDGE,"E33"),sQuery(id+"F0.wireOp",EDGE,"E34"),sQuery(id+"F0.wireOp",EDGE,"E35"),sQuery(id+"F0.wireOp",EDGE,"E36"),sQuery(id+"F0.wireOp",EDGE,"E37"),sQuery(id+"F0.wireOp",EDGE,"E38"),sQuery(id+"F0.wireOp",EDGE,"E39"),sQuery(id+"F0.wireOp",EDGE,"E40"),sQuery(id+"F0.wireOp",EDGE,"E41"),sQuery(id+"F0.wireOp",EDGE,"E42"),sQuery(id+"F0.wireOp",EDGE,"E43"),sQuery(id+"F0.wireOp",EDGE,"E44"),sQuery(id+"F0.wireOp",EDGE,"E45"),sQuery(id+"F0.wireOp",EDGE,"E46"),sQuery(id+"F0.wireOp",EDGE,"E47"),sQuery(id+"F0.wireOp",EDGE,"E48"),sQuery(id+"F0.wireOp",EDGE,"E49"),sQuery(id+"F0.wireOp",EDGE,"E50"),sQuery(id+"F0.wireOp",EDGE,"E51"),sQuery(id+"F0.wireOp",EDGE,"E52"),sQuery(id+"F0.wireOp",EDGE,"E53"),sQuery(id+"F0.wireOp",EDGE,"E54"),sQuery(id+"F0.wireOp",EDGE,"E55"),sQuery(id+"F0.wireOp",EDGE,"E56"),sQuery(id+"F0.wireOp",EDGE,"E57"),sQuery(id+"F0.wireOp",EDGE,"E58"),sQuery(id+"F0.wireOp",EDGE,"E59"),sQuery(id+"F0.wireOp",EDGE,"E60"),sQuery(id+"F0.wireOp",EDGE,"E61"),sQuery(id+"F0.wireOp",EDGE,"E62"),sQuery(id+"F0.wireOp",EDGE,"E63"),sQuery(id+"F0.wireOp",EDGE,"E64"),sQuery(id+"F0.wireOp",EDGE,"E65"),sQuery(id+"F0.wireOp",EDGE,"E66"),sQuery(id+"F0.wireOp",EDGE,"E67"),sQuery(id+"F0.wireOp",EDGE,"E68"),sQuery(id+"F0.wireOp",EDGE,"E69"),sQuery(id+"F0.wireOp",EDGE,"E70"),sQuery(id+"F0.wireOp",EDGE,"E71"),sQuery(id+"F0.wireOp",EDGE,"E72"),sQuery(id+"F0.wireOp",EDGE,"E73"),sQuery(id+"F0.wireOp",EDGE,"E74"),sQuery(id+"F0.wireOp",EDGE,"E75"),sQuery(id+"F0.wireOp",EDGE,"E76"),sQuery(id+"F0.wireOp",EDGE,"E77"),sQuery(id+"F0.wireOp",EDGE,"E78"),sQuery(id+"F0.wireOp",EDGE,"E79"),sQuery(id+"F0.wireOp",EDGE,"E80"),sQuery(id+"F0.wireOp",EDGE,"E81"),sQuery(id+"F0.wireOp",EDGE,"E82"),sQuery(id+"F0.wireOp",EDGE,"E83"),sQuery(id+"F0.wireOp",EDGE,"E84"),sQuery(id+"F0.wireOp",EDGE,"E85"),sQuery(id+"F0.wireOp",EDGE,"E86"),sQuery(id+"F0.wireOp",EDGE,"E87"),sQuery(id+"F0.wireOp",EDGE,"E88"),sQuery(id+"F0.wireOp",EDGE,"E89"),sQuery(id+"F0.wireOp",EDGE,"E90"),sQuery(id+"F0.wireOp",EDGE,"E91"),sQuery(id+"F0.wireOp",EDGE,"E92"),sQuery(id+"F0.wireOp",EDGE,"E93"),sQuery(id+"F0.wireOp",EDGE,"E94"),sQuery(id+"F0.wireOp",EDGE,"E95"),sQuery(id+"F0.wireOp",EDGE,"E96"),sQuery(id+"F0.wireOp",EDGE,"E97"),sQuery(id+"F0.wireOp",EDGE,"E98"),sQuery(id+"F0.wireOp",EDGE,"E99"),sQuery(id+"F0.wireOp",EDGE,"E100"),sQuery(id+"F0.wireOp",EDGE,"E101"),sQuery(id+"F0.wireOp",EDGE,"E102"),sQuery(id+"F0.wireOp",EDGE,"E103"),sQuery(id+"F0.wireOp",EDGE,"E104"),sQuery(id+"F0.wireOp",EDGE,"E105"),sQuery(id+"F0.wireOp",EDGE,"E106"),sQuery(id+"F0.wireOp",EDGE,"E107"),sQuery(id+"F0.wireOp",EDGE,"E108"),sQuery(id+"F0.wireOp",EDGE,"E109"),sQuery(id+"F0.wireOp",EDGE,"E110"),sQuery(id+"F0.wireOp",EDGE,"E111"),sQuery(id+"F0.wireOp",EDGE,"E112"),sQuery(id+"F0.wireOp",EDGE,"E113"),sQuery(id+"F0.wireOp",EDGE,"E114"),sQuery(id+"F0.wireOp",EDGE,"E115"),sQuery(id+"F0.wireOp",EDGE,"E116"),sQuery(id+"F0.wireOp",EDGE,"E117"),sQuery(id+"F0.wireOp",EDGE,"E118"),sQuery(id+"F0.wireOp",EDGE,"E119"),sQuery(id+"F0.wireOp",EDGE,"E120"),sQuery(id+"F0.wireOp",EDGE,"E121"),sQuery(id+"F0.wireOp",EDGE,"E122"),sQuery(id+"F0.wireOp",EDGE,"E123"),sQuery(id+"F0.wireOp",EDGE,"E124"),sQuery(id+"F0.wireOp",EDGE,"E125"),sQuery(id+"F0.wireOp",EDGE,"E126"),sQuery(id+"F0.wireOp",EDGE,"E127"),sQuery(id+"F0.wireOp",EDGE,"E128"),sQuery(id+"F0.wireOp",EDGE,"E129"),sQuery(id+"F0.wireOp",EDGE,"E130"),sQuery(id+"F0.wireOp",EDGE,"E131"),sQuery(id+"F0.wireOp",EDGE,"E132"),sQuery(id+"F0.wireOp",EDGE,"E133"),sQuery(id+"F0.wireOp",EDGE,"E134"),sQuery(id+"F0.wireOp",EDGE,"E135"),sQuery(id+"F0.wireOp",EDGE,"E136"),sQuery(id+"F0.wireOp",EDGE,"E137"),sQuery(id+"F0.wireOp",EDGE,"E138"),sQuery(id+"F0.wireOp",EDGE,"E139"),sQuery(id+"F0.wireOp",EDGE,"E140"),sQuery(id+"F0.wireOp",EDGE,"E141"),sQuery(id+"F0.wireOp",EDGE,"E142"),sQuery(id+"F0.wireOp",EDGE,"E143"),sQuery(id+"F0.wireOp",EDGE,"E144"),sQuery(id+"F0.wireOp",EDGE,"E145"),sQuery(id+"F0.wireOp",EDGE,"E146"),sQuery(id+"F0.wireOp",EDGE,"E147"),sQuery(id+"F0.wireOp",EDGE,"E148"),sQuery(id+"F0.wireOp",EDGE,"E149"),sQuery(id+"F0.wireOp",EDGE,"E150"),sQuery(id+"F0.wireOp",EDGE,"E151"),sQuery(id+"F0.wireOp",EDGE,"E152"),sQuery(id+"F0.wireOp",EDGE,"E153"),sQuery(id+"F0.wireOp",EDGE,"E154"),sQuery(id+"F0.wireOp",EDGE,"E155"),sQuery(id+"F0.wireOp",EDGE,"E156"),sQuery(id+"F0.wireOp",EDGE,"E157"),sQuery(id+"F0.wireOp",EDGE,"E158"),sQuery(id+"F0.wireOp",EDGE,"E159"),sQuery(id+"F0.wireOp",EDGE,"E160"),sQuery(id+"F0.wireOp",EDGE,"E161"),sQuery(id+"F0.wireOp",EDGE,"E162"),sQuery(id+"F0.wireOp",EDGE,"E163"),sQuery(id+"F0.wireOp",EDGE,"E164"),sQuery(id+"F0.wireOp",EDGE,"E165"),sQuery(id+"F0.wireOp",EDGE,"E166"),sQuery(id+"F0.wireOp",EDGE,"E167"),sQuery(id+"F0.wireOp",EDGE,"E168"),sQuery(id+"F0.wireOp",EDGE,"E169"),sQuery(id+"F0.wireOp",EDGE,"E170"),sQuery(id+"F0.wireOp",EDGE,"E171"),sQuery(id+"F0.wireOp",EDGE,"E172"),sQuery(id+"F0.wireOp",EDGE,"E173"),sQuery(id+"F0.wireOp",EDGE,"E174"),sQuery(id+"F0.wireOp",EDGE,"E175"),sQuery(id+"F0.wireOp",EDGE,"E176"),sQuery(id+"F0.wireOp",EDGE,"E177"),sQuery(id+"F0.wireOp",EDGE,"E178"),sQuery(id+"F0.wireOp",EDGE,"E179"),sQuery(id+"F0.wireOp",EDGE,"E180"),sQuery(id+"F0.wireOp",EDGE,"E181"),sQuery(id+"F0.wireOp",EDGE,"E182"),sQuery(id+"F0.wireOp",EDGE,"E183"),sQuery(id+"F0.wireOp",EDGE,"E184"),sQuery(id+"F0.wireOp",EDGE,"E185"),sQuery(id+"F0.wireOp",EDGE,"E186"),sQuery(id+"F0.wireOp",EDGE,"E187"),sQuery(id+"F0.wireOp",EDGE,"E188"),sQuery(id+"F0.wireOp",EDGE,"E189"),sQuery(id+"F0.wireOp",EDGE,"E190"),sQuery(id+"F0.wireOp",EDGE,"E191"),sQuery(id+"F0.wireOp",EDGE,"E192"),sQuery(id+"F0.wireOp",EDGE,"E193"),sQuery(id+"F0.wireOp",EDGE,"E194"),sQuery(id+"F0.wireOp",EDGE,"E195"),sQuery(id+"F0.wireOp",EDGE,"E196"),sQuery(id+"F0.wireOp",EDGE,"E197"),sQuery(id+"F0.wireOp",EDGE,"E198"),sQuery(id+"F0.wireOp",EDGE,"E199"),sQuery(id+"F0.wireOp",EDGE,"E200"),sQuery(id+"F0.wireOp",EDGE,"E201"),sQuery(id+"F0.wireOp",EDGE,"E202"),sQuery(id+"F0.wireOp",EDGE,"E203"),sQuery(id+"F0.wireOp",EDGE,"E204"),sQuery(id+"F0.wireOp",EDGE,"E205"),sQuery(id+"F0.wireOp",EDGE,"E206"),sQuery(id+"F0.wireOp",EDGE,"E207"),sQuery(id+"F0.wireOp",EDGE,"E208"),sQuery(id+"F0.wireOp",EDGE,"E209"),sQuery(id+"F0.wireOp",EDGE,"E210"),sQuery(id+"F0.wireOp",EDGE,"E211"),sQuery(id+"F0.wireOp",EDGE,"E212"),sQuery(id+"F0.wireOp",EDGE,"E213"),sQuery(id+"F0.wireOp",EDGE,"E214"),sQuery(id+"F0.wireOp",EDGE,"E215"),sQuery(id+"F0.wireOp",EDGE,"E216"),sQuery(id+"F0.wireOp",EDGE,"E217"),sQuery(id+"F0.wireOp",EDGE,"E218"),sQuery(id+"F0.wireOp",EDGE,"E219"),sQuery(id+"F0.wireOp",EDGE,"E220"),sQuery(id+"F0.wireOp",EDGE,"E221"),sQuery(id+"F0.wireOp",EDGE,"E222"),sQuery(id+"F0.wireOp",EDGE,"E223"),sQuery(id+"F0.wireOp",EDGE,"E224"),sQuery(id+"F0.wireOp",EDGE,"E225"),sQuery(id+"F0.wireOp",EDGE,"E226"),sQuery(id+"F0.wireOp",EDGE,"E227"),sQuery(id+"F0.wireOp",EDGE,"E228"),sQuery(id+"F0.wireOp",EDGE,"E229"),sQuery(id+"F0.wireOp",EDGE,"E230"),sQuery(id+"F0.wireOp",EDGE,"E231"),sQuery(id+"F0.wireOp",EDGE,"E232"),sQuery(id+"F0.wireOp",EDGE,"E233"),sQuery(id+"F0.wireOp",EDGE,"E234"),sQuery(id+"F0.wireOp",EDGE,"E235"),sQuery(id+"F0.wireOp",EDGE,"E236"),sQuery(id+"F0.wireOp",EDGE,"E237"),sQuery(id+"F0.wireOp",EDGE,"E238"),sQuery(id+"F0.wireOp",EDGE,"E239"),sQuery(id+"F0.wireOp",EDGE,"E240"),sQuery(id+"F0.wireOp",EDGE,"E241"),sQuery(id+"F0.wireOp",EDGE,"E242"),sQuery(id+"F0.wireOp",EDGE,"E243"),sQuery(id+"F0.wireOp",EDGE,"E244"),sQuery(id+"F0.wireOp",EDGE,"E245"),sQuery(id+"F0.wireOp",EDGE,"E246"),sQuery(id+"F0.wireOp",EDGE,"E247"),sQuery(id+"F0.wireOp",EDGE,"E248"),sQuery(id+"F0.wireOp",EDGE,"E249"),sQuery(id+"F0.wireOp",EDGE,"E250"),sQuery(id+"F0.wireOp",EDGE,"E251"),sQuery(id+"F0.wireOp",EDGE,"E252"),sQuery(id+"F0.wireOp",EDGE,"E253"),sQuery(id+"F0.wireOp",EDGE,"E254"),sQuery(id+"F0.wireOp",EDGE,"E255"),sQuery(id+"F0.wireOp",EDGE,"E256"),sQuery(id+"F0.wireOp",EDGE,"E257"),sQuery(id+"F0.wireOp",EDGE,"E258"),sQuery(id+"F0.wireOp",EDGE,"E259"),sQuery(id+"F0.wireOp",EDGE,"E260"),sQuery(id+"F0.wireOp",EDGE,"E261"),sQuery(id+"F0.wireOp",EDGE,"E262"),sQuery(id+"F0.wireOp",EDGE,"E263"),sQuery(id+"F0.wireOp",EDGE,"E264"),sQuery(id+"F0.wireOp",EDGE,"E265"),sQuery(id+"F0.wireOp",EDGE,"E266"),sQuery(id+"F0.wireOp",EDGE,"E267"),sQuery(id+"F0.wireOp",EDGE,"E268"),sQuery(id+"F0.wireOp",EDGE,"E269"),sQuery(id+"F0.wireOp",EDGE,"E270"),sQuery(id+"F0.wireOp",EDGE,"E271"),sQuery(id+"F0.wireOp",EDGE,"E272"),sQuery(id+"F0.wireOp",EDGE,"E273"),sQuery(id+"F0.wireOp",EDGE,"E274"),sQuery(id+"F0.wireOp",EDGE,"E275"),sQuery(id+"F0.wireOp",EDGE,"E276"),sQuery(id+"F0.wireOp",EDGE,"E277"),sQuery(id+"F0.wireOp",EDGE,"E278"),sQuery(id+"F0.wireOp",EDGE,"E279"),sQuery(id+"F0.wireOp",EDGE,"E280"),sQuery(id+"F0.wireOp",EDGE,"E281"),sQuery(id+"F0.wireOp",EDGE,"E282"),sQuery(id+"F0.wireOp",EDGE,"E283"),sQuery(id+"F0.wireOp",EDGE,"E284"),sQuery(id+"F0.wireOp",EDGE,"E285"),sQuery(id+"F0.wireOp",EDGE,"E286"),sQuery(id+"F0.wireOp",EDGE,"E287"),sQuery(id+"F0.wireOp",EDGE,"E288"),sQuery(id+"F0.wireOp",EDGE,"E289"),sQuery(id+"F0.wireOp",EDGE,"E290"),sQuery(id+"F0.wireOp",EDGE,"E291"),sQuery(id+"F0.wireOp",EDGE,"E292"),sQuery(id+"F0.wireOp",EDGE,"E293"),sQuery(id+"F0.wireOp",EDGE,"E294"),sQuery(id+"F0.wireOp",EDGE,"E295"),sQuery(id+"F0.wireOp",EDGE,"E296"),sQuery(id+"F0.wireOp",EDGE,"E297"),sQuery(id+"F0.wireOp",EDGE,"E298"),sQuery(id+"F0.wireOp",EDGE,"E299"),sQuery(id+"F0.wireOp",EDGE,"E300"),sQuery(id+"F0.wireOp",EDGE,"E301"),sQuery(id+"F0.wireOp",EDGE,"E302"),sQuery(id+"F0.wireOp",EDGE,"E303"),sQuery(id+"F0.wireOp",EDGE,"E304"),sQuery(id+"F0.wireOp",EDGE,"E305"),sQuery(id+"F0.wireOp",EDGE,"E306"),sQuery(id+"F0.wireOp",EDGE,"E307"),sQuery(id+"F0.wireOp",EDGE,"E308"),sQuery(id+"F0.wireOp",EDGE,"E309"),sQuery(id+"F0.wireOp",EDGE,"E310"),sQuery(id+"F0.wireOp",EDGE,"E311"),sQuery(id+"F0.wireOp",EDGE,"E312"),sQuery(id+"F0.wireOp",EDGE,"E313"),sQuery(id+"F0.wireOp",EDGE,"E314"),sQuery(id+"F0.wireOp",EDGE,"E315"),sQuery(id+"F0.wireOp",EDGE,"E316"),sQuery(id+"F0.wireOp",EDGE,"E317"),sQuery(id+"F0.wireOp",EDGE,"E318"),sQuery(id+"F0.wireOp",EDGE,"E319"),sQuery(id+"F0.wireOp",EDGE,"E320"),sQuery(id+"F0.wireOp",EDGE,"E321"),sQuery(id+"F0.wireOp",EDGE,"E322"),sQuery(id+"F0.wireOp",EDGE,"E323"),sQuery(id+"F0.wireOp",EDGE,"E324"),sQuery(id+"F0.wireOp",EDGE,"E325"),sQuery(id+"F0.wireOp",EDGE,"E326"),sQuery(id+"F0.wireOp",EDGE,"E327"),sQuery(id+"F0.wireOp",EDGE,"E328"),sQuery(id+"F0.wireOp",EDGE,"E329"),sQuery(id+"F0.wireOp",EDGE,"E330"),sQuery(id+"F0.wireOp",EDGE,"E331"),sQuery(id+"F0.wireOp",EDGE,"E332"),sQuery(id+"F0.wireOp",EDGE,"E333"),sQuery(id+"F0.wireOp",EDGE,"E334"),sQuery(id+"F0.wireOp",EDGE,"E335"),sQuery(id+"F0.wireOp",EDGE,"E336"),sQuery(id+"F0.wireOp",EDGE,"E337"),sQuery(id+"F0.wireOp",EDGE,"E338"),sQuery(id+"F0.wireOp",EDGE,"E339")])],"isStart":true});
            var sketch = newSketch(context, id + "F2", { "sketchPlane" : qUnion([Q0])});
            skLineSegment(sketch, "E340", {"start": v(-53.91, -26.5) * mm, "end": v(-26.96, -42.1) * mm});
            skLineSegment(sketch, "E341", {"start": v(-26.96, -42.1) * mm, "end": v(0, -32.6) * mm});
            skLineSegment(sketch, "E342", {"start": v(0, -32.6) * mm, "end": v(-10.1, -10.9) * mm});
            skLineSegment(sketch, "E343", {"start": v(-10.1, -10.9) * mm, "end": v(-53.91, -20.45) * mm});
            skLineSegment(sketch, "E344", {"start": v(-53.91, -20.45) * mm, "end": v(-53.91, -26.5) * mm});
            skLineSegment(sketch, "E345", {"start": v(-53.91, -26.5) * mm, "end": v(-53.91, -42.1) * mm});
            skLineSegment(sketch, "E346", {"start": v(-53.91, -42.1) * mm, "end": v(-26.96, -42.1) * mm});
            skLineSegment(sketch, "E347", {"start": v(0, -42.1) * mm, "end": v(0, -10.9) * mm});
            skLineSegment(sketch, "E348", {"start": v(0, -10.9) * mm, "end": v(-53.91, -10.9) * mm});
            skLineSegment(sketch, "E349", {"start": v(-53.91, -10.9) * mm, "end": v(-53.91, -26.5) * mm});
            skSolve(sketch);
        }
        {
            var Q0;
            {var subQ0=sQuery(id+"F2.wireOp",EDGE,"E343");Q0=makeQuery(id+"F2.imprint","IMPRINT",FACE,{"disambiguationData":[TD([[makeQuery(id+"F2.imprint","IMPRINT",EDGE,{"derivedFrom":subQ0}),-1.0]])]});}
            var Q1;
            {var subQ0=sQuery(id+"F2.wireOp",EDGE,"E342");Q1=makeQuery(id+"F2.imprint","IMPRINT",FACE,{"disambiguationData":[TD([[makeQuery(id+"F2.imprint","IMPRINT",EDGE,{"derivedFrom":subQ0}),-1.0]])]});}
            var Q2;
            {var subQ0=sQuery(id+"F2.wireOp",EDGE,"E341");Q2=makeQuery(id+"F2.imprint","IMPRINT",FACE,{"disambiguationData":[TD([[makeQuery(id+"F2.imprint","IMPRINT",EDGE,{"derivedFrom":subQ0}),-1.0]])]});}
            var Q3;
            Q3=makeQuery(id+"F2.imprint","IMPRINT",FACE,{"disambiguationData":[TD([[makeQuery(id+"F2.imprint","IMPRINT",EDGE,{"derivedFrom":sQuery(id+"F2.wireOp",EDGE,"E340")}),-1.0]])]});
            extrude(context, id + "F3", {"entities" : qUnion([Q0, Q1, Q2, Q3]), "operationType" : NewBodyOperationType.REMOVE, "oppositeDirection" : true, "depth" : 25.4 * mm, "offsetDistance" : 25.4 * mm});
        }
    });
